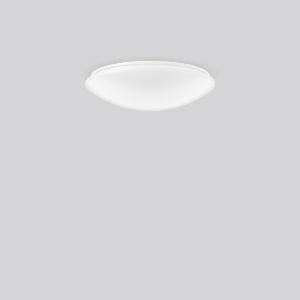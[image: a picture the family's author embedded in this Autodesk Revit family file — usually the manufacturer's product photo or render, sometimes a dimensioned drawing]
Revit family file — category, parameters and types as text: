
# Revit family: flat_polymero_311523_002_7_76_8568
name_source: partatom
category: Lighting Fixtures
units: mm (PartAtom-declared; Revit-internal decimal feet)

## family parameters
Cut with Voids When Loaded = No
Host = Face
Light Source = No
Part Type = Normal
Room Calculation Point = No
Round Connector Dimension = Use Diameter
Shared = No

## types (1)
- FLAT POLYMERO (1 x LED Modul 830, 1450 lm, 3000)
    Apparent Load = 14 VA
    CIE Flux Codes = 43 72 90 88 100
    Color Rendering = 80
    Color Temperature = 3000
    Default Elevation = 1800 mm
    Description = Series: FLAT POLYMERO
Decorative round surface-mounted luminaire. Base: metal, powder-coated. Diffuser made of non-yellowing plastic (PMMA), opal. Diffuser fastening: patented push system. Suitable for Ceiling mounting, Wall (surface). 
Colour: white
Diameter: 360 mm
Height: 100 mm
Lamp: LED
Socket: without socket
Colour temperature: 3000K
Colour rendering index (CRI): 80
System power: 14 W
Rated luminous flux: 1450 lm
Beam angle Down: 116°
Luminous efficiency: 104 lm/W
Control gear: Converter, dimmable, DALI
Protection class: I
Type of protection: IP 40
    Height = 100 mm  [stored 0.328084 ft]
    Lamp = 1 x LED Modul 830
    Lamp Light Flux = 1450 lm
    Lamp count = 1
    Length = 360 mm
    Lifetime = 50000 h
    Luminous efficacy = 104 lm/W
    Manufacturer = RZB
    ModVariant = No
    Model = 311523.002.7.76
    Mounting Place = Ceiling, Wall
    Mounting Type = Surface mounted
    Number of Poles = 1
    OnlyDefault = Yes
    Power Factor = 1
    Product Name = FLAT POLYMERO
    Product group = Surface mounted ceiling and wall luminaires
    ProductGroupID = 305
    Protection Class = Protection class I
    Protection Degree = IP 40
    RLX_Detail_Level = 1
    RLX_Emergency_Light_Flux = 0 lm
    RLX_Emergency_Type = 0
    RLX_Emergency_Type_DB = No
    RlxData = <blob elided: 76653 chars, md5=fe44cbd5>
    Socket = socket
    Standby Power = 0 W
    System Light Flux = 1450 lm
    System Power = 14 W
    Type Comments = ALEA SPOT
    Type Image = 311523.002.1.jpg
    URL = http://relux.com
    VarID = ---
    Voltage = 230 V
    Voltage Range = 220-240 V
    Weight = 0.00 kg
    Width = 0 mm  [stored 0 ft]

note: [stored X ft] marks values corroborated as IEEE doubles in the binary element streams (Revit-internal decimal feet)

## geometry (parser evidence)
native form markers: Blend x4, Sweep x12
no freeform markers — native parametric forms only
